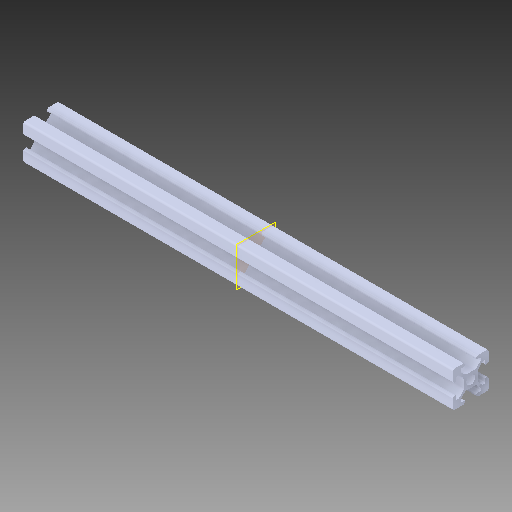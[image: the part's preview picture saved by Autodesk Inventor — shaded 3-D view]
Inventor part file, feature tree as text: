
AUTODESK INVENTOR PART (.ipt)
format: ipt  version: 2018 (Build 220112000, 112)  size: 366,592 bytes
history: native  units: in
note: dims shown in document units (in); Inventor stores cm internally (conversion verified against a paired STEP export)
features: extrude x1, plane x1, sketch x1, projected_geometry x1, fillet x1
ambient origin geometry x8: Origin, YZ Plane, XZ Plane, XY Plane, X Axis, Y Axis, Z Axis, Center Point
bodies: Solid1 (feature_tree)
feature tree (5):
  extrude  "Extrusion2"  [1 undecoded]
  plane  "Work Plane1"
  sketch  "Sketch3"  dims[d2=5.5118in d3=0.0in]
  projected_geometry  "Projected Loop2"
  fillet  "Fillet5"  [1 undecoded]
note: 2 required parameter values undecoded (feature->parameter linkage not recoverable at this tier; creation-order binding heuristic only, values carry confidence <= 0.55)
